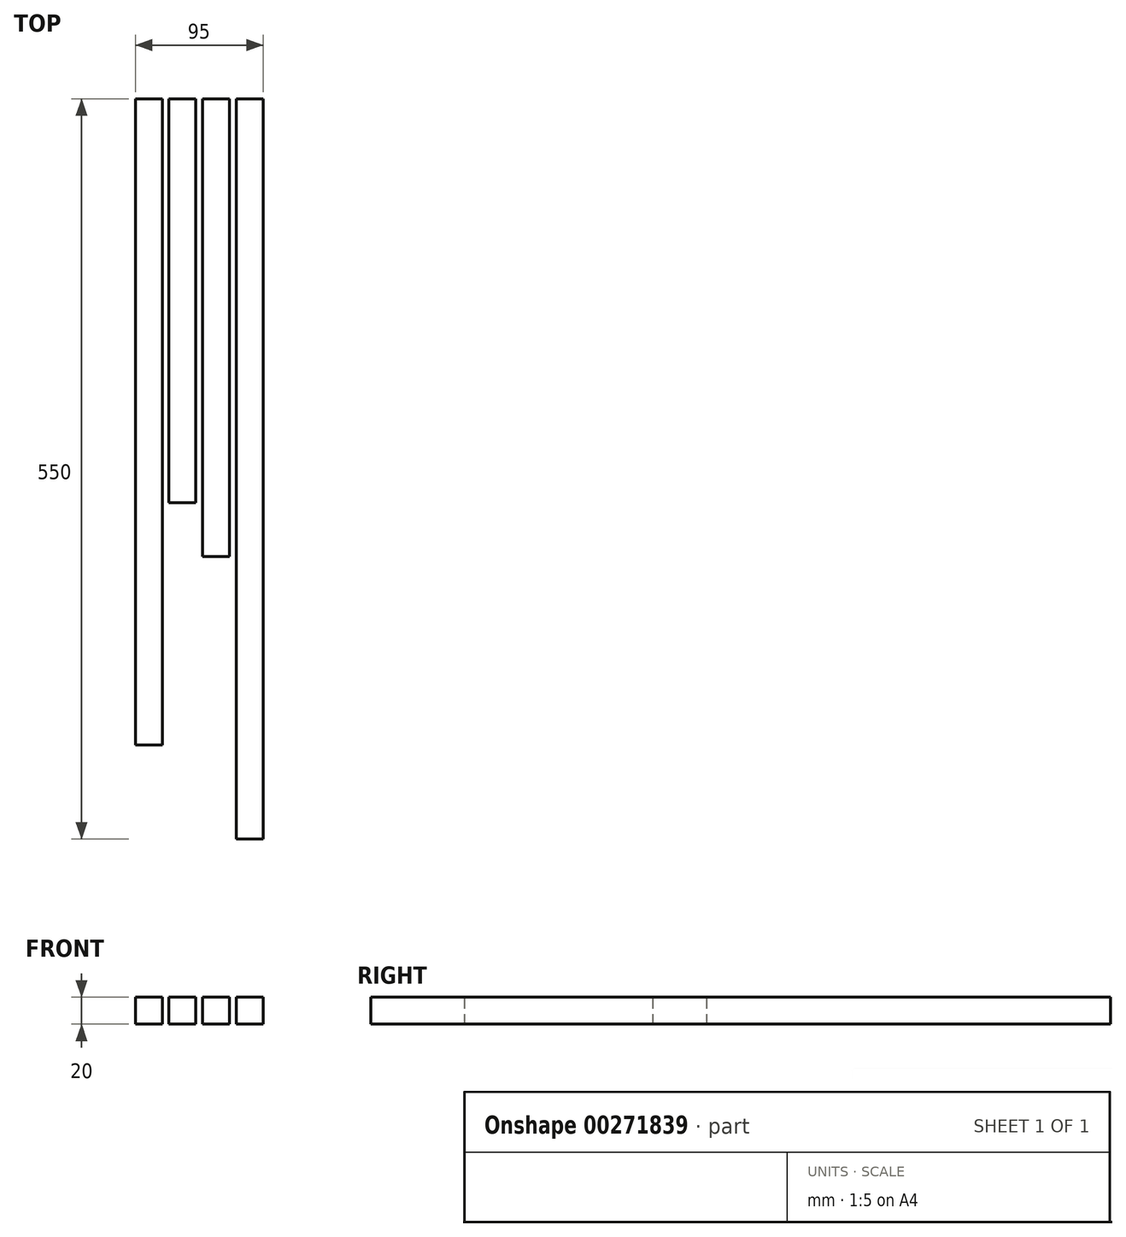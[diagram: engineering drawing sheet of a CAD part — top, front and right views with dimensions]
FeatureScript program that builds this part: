
annotation { "Feature Type Name" : "Feature", "Feature Type Description" : "" }
export const myFeature = defineFeature(function(context is Context, id is Id, definition is map)
    precondition{}
    {
        {
            var Q0;
            Q0=qCreatedBy(makeId("Front.planeOp"),FACE);
            var sketch = newSketch(context, id + "F0", { "sketchPlane" : qUnion([Q0])});
            skLineSegment(sketch, "E0.bottom", {"start": v(0, 0) * mm, "end": v(20, 0) * mm});
            skLineSegment(sketch, "E0.top", {"start": v(0, 20) * mm, "end": v(20, 20) * mm});
            skLineSegment(sketch, "E0.left", {"start": v(0, 0) * mm, "end": v(0, 20) * mm});
            skLineSegment(sketch, "E0.right", {"start": v(20, 0) * mm, "end": v(20, 20) * mm});
            skLineSegment(sketch, "E1.1.0.0", {"start": v(25, 20) * mm, "end": v(45, 20) * mm});
            skLineSegment(sketch, "E1.1.0.1", {"start": v(25, 0) * mm, "end": v(25, 20) * mm});
            skLineSegment(sketch, "E1.1.0.2", {"start": v(45, 0) * mm, "end": v(45, 20) * mm});
            skLineSegment(sketch, "E1.1.0.3", {"start": v(25, 0) * mm, "end": v(45, 0) * mm});
            skLineSegment(sketch, "E1.2.0.0", {"start": v(50, 20) * mm, "end": v(70, 20) * mm});
            skLineSegment(sketch, "E1.2.0.1", {"start": v(50, 0) * mm, "end": v(50, 20) * mm});
            skLineSegment(sketch, "E1.2.0.2", {"start": v(70, 0) * mm, "end": v(70, 20) * mm});
            skLineSegment(sketch, "E1.2.0.3", {"start": v(50, 0) * mm, "end": v(70, 0) * mm});
            skLineSegment(sketch, "E1.3.0.0", {"start": v(75, 20) * mm, "end": v(95, 20) * mm});
            skLineSegment(sketch, "E1.3.0.1", {"start": v(75, 0) * mm, "end": v(75, 20) * mm});
            skLineSegment(sketch, "E1.3.0.2", {"start": v(95, 0) * mm, "end": v(95, 20) * mm});
            skLineSegment(sketch, "E1.3.0.3", {"start": v(75, 0) * mm, "end": v(95, 0) * mm});
            skLineSegment(sketch, "E1.4.0.0", {"start": v(100, 20) * mm, "end": v(120, 20) * mm});
            skLineSegment(sketch, "E1.4.0.1", {"start": v(100, 0) * mm, "end": v(100, 20) * mm});
            skLineSegment(sketch, "E1.4.0.2", {"start": v(120, 0) * mm, "end": v(120, 20) * mm});
            skLineSegment(sketch, "E1.4.0.3", {"start": v(100, 0) * mm, "end": v(120, 0) * mm});
            skLineSegment(sketch, "E1.5.0.0", {"start": v(125, 20) * mm, "end": v(145, 20) * mm});
            skLineSegment(sketch, "E1.5.0.1", {"start": v(125, 0) * mm, "end": v(125, 20) * mm});
            skLineSegment(sketch, "E1.5.0.2", {"start": v(145, 0) * mm, "end": v(145, 20) * mm});
            skLineSegment(sketch, "E1.5.0.3", {"start": v(125, 0) * mm, "end": v(145, 0) * mm});
            skLineSegment(sketch, "E1.direction1", {"start": v(0, 0) * mm, "end": v(25, 0) * mm, "construction": true});
            skSolve(sketch);
        }
        {
            var Q0;
            Q0=makeQuery(id+"F0.imprint","IMPRINT",FACE,{"disambiguationData":[TD([[makeQuery(id+"F0.imprint","IMPRINT",EDGE,{"derivedFrom":sQuery(id+"F0.wireOp",EDGE,"E0.bottom")}),1.0]])]});
            extrude(context, id + "F1", {"entities" : qUnion([Q0]), "depth" : 480 * mm});
        }
        {
            var Q0;
            Q0=makeQuery(id+"F0.imprint","IMPRINT",FACE,{"disambiguationData":[TD([[makeQuery(id+"F0.imprint","IMPRINT",EDGE,{"derivedFrom":sQuery(id+"F0.wireOp",EDGE,"E1.1.0.0")}),-1.0]])]});
            extrude(context, id + "F2", {"entities" : qUnion([Q0]), "depth" : 300 * mm});
        }
        {
            var Q0;
            Q0=makeQuery(id+"F0.imprint","IMPRINT",FACE,{"disambiguationData":[TD([[makeQuery(id+"F0.imprint","IMPRINT",EDGE,{"derivedFrom":sQuery(id+"F0.wireOp",EDGE,"E1.2.0.0")}),-1.0]])]});
            extrude(context, id + "F3", {"entities" : qUnion([Q0]), "depth" : 340 * mm});
        }
        {
            var Q0;
            Q0=makeQuery(id+"F0.imprint","IMPRINT",FACE,{"disambiguationData":[TD([[makeQuery(id+"F0.imprint","IMPRINT",EDGE,{"derivedFrom":sQuery(id+"F0.wireOp",EDGE,"E1.3.0.0")}),-1.0]])]});
            extrude(context, id + "F4", {"entities" : qUnion([Q0]), "depth" : 550 * mm});
        }
    });
